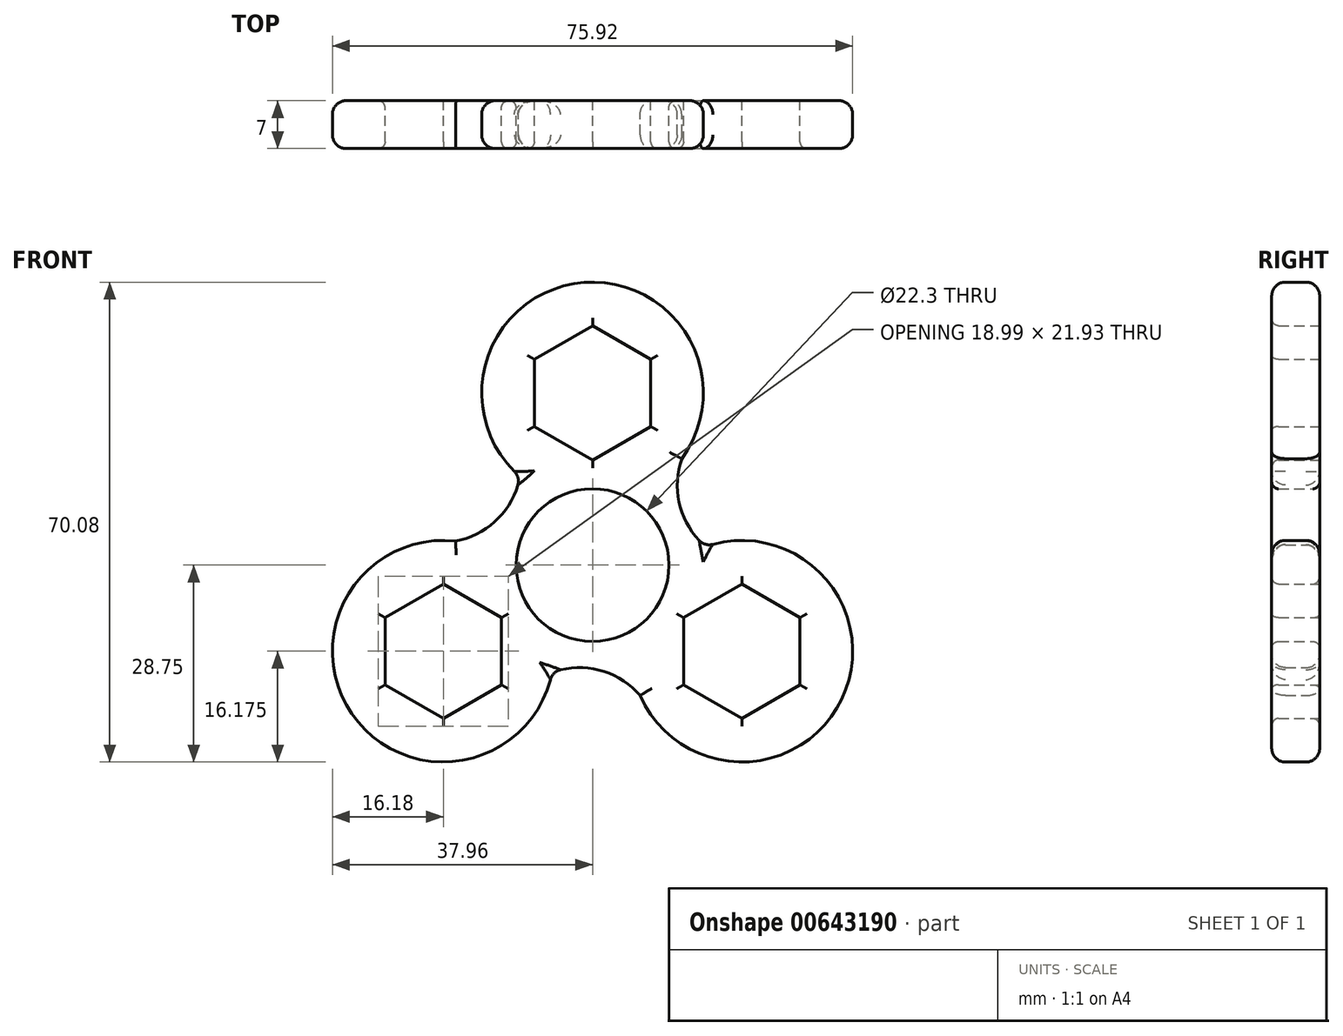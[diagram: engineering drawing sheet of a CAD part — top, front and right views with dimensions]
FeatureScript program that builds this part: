
annotation { "Feature Type Name" : "Feature", "Feature Type Description" : "" }
export const myFeature = defineFeature(function(context is Context, id is Id, definition is map)
    precondition{}
    {
        {
            var Q0;
            Q0=qCreatedBy(makeId("Front.planeOp"),FACE);
            var sketch = newSketch(context, id + "F0", { "sketchPlane" : qUnion([Q0])});
            skLineSegment(sketch, "E0", {"start": v(0, 25) * mm, "end": v(0, 0) * mm});
            skLineSegment(sketch, "E1.1.0", {"start": v(-21.65, -12.5) * mm, "end": v(0, 0) * mm});
            skLineSegment(sketch, "E1.2.0", {"start": v(21.65, -12.5) * mm, "end": v(0, 0) * mm});
            skPoint(sketch, "E1.center", {"position": v(0, 0) * mm});
            skCircle(sketch, "E2", {"center": v(0, 0) * mm, "radius": 11.15 * mm});
            skCircle(sketch, "E3.cCircle", {"center": v(0, 25.15) * mm, "radius": 8.5 * mm, "construction": true});
            skLineSegment(sketch, "E3.0", {"start": v(8.5, 30.05) * mm, "end": v(8.5, 20.24) * mm});
            skLineSegment(sketch, "E3.1", {"start": v(8.5, 20.24) * mm, "end": v(0, 15.34) * mm});
            skLineSegment(sketch, "E3.2", {"start": v(0, 15.34) * mm, "end": v(-8.5, 20.24) * mm});
            skLineSegment(sketch, "E3.3", {"start": v(-8.5, 20.24) * mm, "end": v(-8.5, 30.05) * mm});
            skLineSegment(sketch, "E3.4", {"start": v(-8.5, 30.05) * mm, "end": v(0, 34.96) * mm});
            skLineSegment(sketch, "E3.5", {"start": v(0, 34.96) * mm, "end": v(8.5, 30.05) * mm});
            skPoint(sketch, "E3.0.midPoint", {"position": v(8.5, 25.15) * mm});
            skCircle(sketch, "E4", {"center": v(0, 25.15) * mm, "radius": 16.18 * mm});
            skCircle(sketch, "E5.1.0", {"center": v(-21.78, -12.57) * mm, "radius": 8.5 * mm, "construction": true});
            skCircle(sketch, "E5.1.1", {"center": v(-21.78, -12.57) * mm, "radius": 16.18 * mm});
            skPoint(sketch, "E5.1.2", {"position": v(-26.03, -5.22) * mm});
            skLineSegment(sketch, "E5.1.3", {"start": v(-21.78, -2.77) * mm, "end": v(-13.28, -7.67) * mm});
            skLineSegment(sketch, "E5.1.4", {"start": v(-30.27, -7.67) * mm, "end": v(-21.78, -2.77) * mm});
            skLineSegment(sketch, "E5.1.5", {"start": v(-13.28, -7.67) * mm, "end": v(-13.28, -17.48) * mm});
            skLineSegment(sketch, "E5.1.6", {"start": v(-13.28, -17.48) * mm, "end": v(-21.78, -22.38) * mm});
            skLineSegment(sketch, "E5.1.7", {"start": v(-21.78, -22.38) * mm, "end": v(-30.27, -17.48) * mm});
            skLineSegment(sketch, "E5.1.8", {"start": v(-30.27, -17.48) * mm, "end": v(-30.27, -7.67) * mm});
            skCircle(sketch, "E5.2.0", {"center": v(21.78, -12.57) * mm, "radius": 8.5 * mm, "construction": true});
            skCircle(sketch, "E5.2.1", {"center": v(21.78, -12.57) * mm, "radius": 16.18 * mm});
            skPoint(sketch, "E5.2.2", {"position": v(17.53, -19.93) * mm});
            skLineSegment(sketch, "E5.2.3", {"start": v(13.28, -17.48) * mm, "end": v(13.28, -7.67) * mm});
            skLineSegment(sketch, "E5.2.4", {"start": v(21.78, -22.38) * mm, "end": v(13.28, -17.48) * mm});
            skLineSegment(sketch, "E5.2.5", {"start": v(13.28, -7.67) * mm, "end": v(21.78, -2.77) * mm});
            skLineSegment(sketch, "E5.2.6", {"start": v(21.78, -2.77) * mm, "end": v(30.27, -7.67) * mm});
            skLineSegment(sketch, "E5.2.7", {"start": v(30.27, -7.67) * mm, "end": v(30.27, -17.48) * mm});
            skLineSegment(sketch, "E5.2.8", {"start": v(30.27, -17.48) * mm, "end": v(21.78, -22.38) * mm});
            skArc(sketch, "E6", {"start": v(-19.97, 3.5) * mm, "mid": v(-13.83, 6.77) * mm, "end": v(-10.6, 12.93) * mm});
            skArc(sketch, "E7.1.0", {"start": v(6.95, -19.05) * mm, "mid": v(1.05, -15.36) * mm, "end": v(-5.9, -15.65) * mm});
            skArc(sketch, "E7.2.0", {"start": v(13.02, 15.55) * mm, "mid": v(12.78, 8.6) * mm, "end": v(16.5, 2.72) * mm});
            skSolve(sketch);
        }
        {
            var Q0;
            Q0=makeQuery(id+"F0.imprint","IMPRINT",FACE,{"disambiguationData":[TD([[makeQuery(id+"F0.imprint","IMPRINT",EDGE,{"derivedFrom":sQuery(id+"F0.wireOp",EDGE,"E3.0")}),1.0]])]});
            var Q1;
            {var subQ5=sQuery(id+"F0.wireOp",EDGE,"E7.2.0");Q1=makeQuery(id+"F0.imprint","IMPRINT",FACE,{"disambiguationData":[TD([[makeQuery(id+"F0.imprint","IMPRINT",EDGE,{"derivedFrom":subQ5}),-1.0]])]});}
            var Q2;
            Q2=makeQuery(id+"F0.imprint","IMPRINT",FACE,{"disambiguationData":[TD([[makeQuery(id+"F0.imprint","IMPRINT",EDGE,{"derivedFrom":sQuery(id+"F0.wireOp",EDGE,"E5.2.3")}),1.0]])]});
            var Q3;
            {var subQ5=sQuery(id+"F0.wireOp",EDGE,"E7.1.0");Q3=makeQuery(id+"F0.imprint","IMPRINT",FACE,{"disambiguationData":[TD([[makeQuery(id+"F0.imprint","IMPRINT",EDGE,{"derivedFrom":subQ5}),-1.0]])]});}
            var Q4;
            {var subQ5=sQuery(id+"F0.wireOp",EDGE,"E6");Q4=makeQuery(id+"F0.imprint","IMPRINT",FACE,{"disambiguationData":[TD([[makeQuery(id+"F0.imprint","IMPRINT",EDGE,{"derivedFrom":subQ5}),-1.0]])]});}
            var Q5;
            Q5=makeQuery(id+"F0.imprint","IMPRINT",FACE,{"disambiguationData":[TD([[makeQuery(id+"F0.imprint","IMPRINT",EDGE,{"derivedFrom":sQuery(id+"F0.wireOp",EDGE,"E5.1.3")}),1.0]])]});
            extrude(context, id + "F1", {"entities" : qUnion([Q0, Q1, Q2, Q3, Q4, Q5]), "endBound" : BoundingType.SYMMETRIC, "depth" : 7 * mm, "offsetDistance" : 25 * mm});
        }
        {
            var Q0;
            Q0=makeQuery(id+"F1.opExtrude","CAP_EDGE",EDGE,{"disambiguationData":[OSD([sQuery(id+"F0.wireOp",EDGE,"E4")])],"isStart":true});
            var Q1;
            Q1=makeQuery(id+"F1.opExtrude","CAP_EDGE",EDGE,{"disambiguationData":[OSD([sQuery(id+"F0.wireOp",EDGE,"E7.2.0")])],"isStart":true});
            var Q2;
            Q2=makeQuery(id+"F1.opExtrude","CAP_EDGE",EDGE,{"disambiguationData":[OSD([sQuery(id+"F0.wireOp",EDGE,"E5.2.1")])],"isStart":true});
            var Q3;
            Q3=makeQuery(id+"F1.opExtrude","CAP_EDGE",EDGE,{"disambiguationData":[OSD([sQuery(id+"F0.wireOp",EDGE,"E7.1.0")])],"isStart":true});
            var Q4;
            Q4=makeQuery(id+"F1.opExtrude","CAP_EDGE",EDGE,{"disambiguationData":[OSD([sQuery(id+"F0.wireOp",EDGE,"E5.1.1")])],"isStart":true});
            var Q5;
            Q5=makeQuery(id+"F1.opExtrude","CAP_EDGE",EDGE,{"disambiguationData":[OSD([sQuery(id+"F0.wireOp",EDGE,"E6")])],"isStart":true});
            fillet(context, id + "F2", {"entities" : qUnion([Q0, Q1, Q2, Q3, Q4, Q5]), "radius" : 2 * mm, "tangentPropagation" : true, "allowEdgeOverflow" : false});
        }
        {
            var Q0;
            Q0=makeQuery(id+"F1.opExtrude","CAP_EDGE",EDGE,{"disambiguationData":[OSD([sQuery(id+"F0.wireOp",EDGE,"E7.2.0")])],"isStart":false});
            var Q1;
            Q1=makeQuery(id+"F1.opExtrude","CAP_EDGE",EDGE,{"disambiguationData":[OSD([sQuery(id+"F0.wireOp",EDGE,"E5.2.1")])],"isStart":false});
            var Q2;
            Q2=makeQuery(id+"F1.opExtrude","CAP_EDGE",EDGE,{"disambiguationData":[OSD([sQuery(id+"F0.wireOp",EDGE,"E7.1.0")])],"isStart":false});
            var Q3;
            Q3=makeQuery(id+"F1.opExtrude","CAP_EDGE",EDGE,{"disambiguationData":[OSD([sQuery(id+"F0.wireOp",EDGE,"E5.1.1")])],"isStart":false});
            var Q4;
            Q4=makeQuery(id+"F1.opExtrude","CAP_EDGE",EDGE,{"disambiguationData":[OSD([sQuery(id+"F0.wireOp",EDGE,"E6")])],"isStart":false});
            var Q5;
            Q5=makeQuery(id+"F1.opExtrude","CAP_EDGE",EDGE,{"disambiguationData":[OSD([sQuery(id+"F0.wireOp",EDGE,"E4")])],"isStart":false});
            fillet(context, id + "F3", {"entities" : qUnion([Q0, Q1, Q2, Q3, Q4, Q5]), "radius" : 2 * mm, "tangentPropagation" : true, "allowEdgeOverflow" : false});
        }
        {
            var Q0;
            Q0=makeQuery(id+"F1.opExtrude","SWEPT_EDGE",EDGE,{"disambiguationData":[OSD([sQuery(id+"F0.wireOp",EDGE,"E5.1.1"),sQuery(id+"F0.wireOp",EDGE,"E7.1.0")])]});
            var Q1;
            Q1=makeQuery(id+"F1.opExtrude","SWEPT_EDGE",EDGE,{"disambiguationData":[OSD([sQuery(id+"F0.wireOp",EDGE,"E5.2.1"),sQuery(id+"F0.wireOp",EDGE,"E7.2.0")])]});
            var Q2;
            Q2=makeQuery(id+"F1.opExtrude","SWEPT_EDGE",EDGE,{"disambiguationData":[OSD([sQuery(id+"F0.wireOp",EDGE,"E4"),sQuery(id+"F0.wireOp",EDGE,"E6")])]});
            fillet(context, id + "F4", {"entities" : qUnion([Q0, Q1, Q2]), "radius" : 2 * mm, "tangentPropagation" : true, "allowEdgeOverflow" : false});
        }
        {
            var Q0;
            Q0=makeQuery(id+"F1.opExtrude","CAP_EDGE",EDGE,{"disambiguationData":[OSD([sQuery(id+"F0.wireOp",EDGE,"E2")])],"isStart":false});
            var Q1;
            Q1=makeQuery(id+"F1.opExtrude","CAP_EDGE",EDGE,{"disambiguationData":[OSD([sQuery(id+"F0.wireOp",EDGE,"E3.4")])],"isStart":false});
            var Q2;
            Q2=makeQuery(id+"F1.opExtrude","CAP_EDGE",EDGE,{"disambiguationData":[OSD([sQuery(id+"F0.wireOp",EDGE,"E3.5")])],"isStart":false});
            var Q3;
            Q3=makeQuery(id+"F1.opExtrude","CAP_EDGE",EDGE,{"disambiguationData":[OSD([sQuery(id+"F0.wireOp",EDGE,"E3.3")])],"isStart":false});
            var Q4;
            Q4=makeQuery(id+"F1.opExtrude","CAP_EDGE",EDGE,{"disambiguationData":[OSD([sQuery(id+"F0.wireOp",EDGE,"E3.2")])],"isStart":false});
            var Q5;
            Q5=makeQuery(id+"F1.opExtrude","CAP_EDGE",EDGE,{"disambiguationData":[OSD([sQuery(id+"F0.wireOp",EDGE,"E3.1")])],"isStart":false});
            var Q6;
            Q6=makeQuery(id+"F1.opExtrude","CAP_EDGE",EDGE,{"disambiguationData":[OSD([sQuery(id+"F0.wireOp",EDGE,"E3.0")])],"isStart":false});
            var Q7;
            Q7=makeQuery(id+"F1.opExtrude","CAP_EDGE",EDGE,{"disambiguationData":[OSD([sQuery(id+"F0.wireOp",EDGE,"E5.2.5")])],"isStart":false});
            var Q8;
            Q8=makeQuery(id+"F1.opExtrude","CAP_EDGE",EDGE,{"disambiguationData":[OSD([sQuery(id+"F0.wireOp",EDGE,"E5.2.6")])],"isStart":false});
            var Q9;
            Q9=makeQuery(id+"F1.opExtrude","CAP_EDGE",EDGE,{"disambiguationData":[OSD([sQuery(id+"F0.wireOp",EDGE,"E5.2.3")])],"isStart":false});
            var Q10;
            Q10=makeQuery(id+"F1.opExtrude","CAP_EDGE",EDGE,{"disambiguationData":[OSD([sQuery(id+"F0.wireOp",EDGE,"E5.2.4")])],"isStart":false});
            var Q11;
            Q11=makeQuery(id+"F1.opExtrude","CAP_EDGE",EDGE,{"disambiguationData":[OSD([sQuery(id+"F0.wireOp",EDGE,"E5.2.8")])],"isStart":false});
            var Q12;
            Q12=makeQuery(id+"F1.opExtrude","CAP_EDGE",EDGE,{"disambiguationData":[OSD([sQuery(id+"F0.wireOp",EDGE,"E5.2.7")])],"isStart":false});
            var Q13;
            Q13=makeQuery(id+"F1.opExtrude","CAP_EDGE",EDGE,{"disambiguationData":[OSD([sQuery(id+"F0.wireOp",EDGE,"E5.1.4")])],"isStart":false});
            var Q14;
            Q14=makeQuery(id+"F1.opExtrude","CAP_EDGE",EDGE,{"disambiguationData":[OSD([sQuery(id+"F0.wireOp",EDGE,"E5.1.3")])],"isStart":false});
            var Q15;
            Q15=makeQuery(id+"F1.opExtrude","CAP_EDGE",EDGE,{"disambiguationData":[OSD([sQuery(id+"F0.wireOp",EDGE,"E5.1.8")])],"isStart":false});
            var Q16;
            Q16=makeQuery(id+"F1.opExtrude","CAP_EDGE",EDGE,{"disambiguationData":[OSD([sQuery(id+"F0.wireOp",EDGE,"E5.1.7")])],"isStart":false});
            var Q17;
            Q17=makeQuery(id+"F1.opExtrude","CAP_EDGE",EDGE,{"disambiguationData":[OSD([sQuery(id+"F0.wireOp",EDGE,"E5.1.6")])],"isStart":false});
            var Q18;
            Q18=makeQuery(id+"F1.opExtrude","CAP_EDGE",EDGE,{"disambiguationData":[OSD([sQuery(id+"F0.wireOp",EDGE,"E2")])],"isStart":true});
            var Q19;
            Q19=makeQuery(id+"F1.opExtrude","CAP_EDGE",EDGE,{"disambiguationData":[OSD([sQuery(id+"F0.wireOp",EDGE,"E5.1.6")])],"isStart":true});
            var Q20;
            Q20=makeQuery(id+"F1.opExtrude","CAP_EDGE",EDGE,{"disambiguationData":[OSD([sQuery(id+"F0.wireOp",EDGE,"E5.1.7")])],"isStart":true});
            var Q21;
            Q21=makeQuery(id+"F1.opExtrude","CAP_EDGE",EDGE,{"disambiguationData":[OSD([sQuery(id+"F0.wireOp",EDGE,"E5.1.8")])],"isStart":true});
            var Q22;
            Q22=makeQuery(id+"F1.opExtrude","CAP_EDGE",EDGE,{"disambiguationData":[OSD([sQuery(id+"F0.wireOp",EDGE,"E5.1.4")])],"isStart":true});
            var Q23;
            Q23=makeQuery(id+"F1.opExtrude","CAP_EDGE",EDGE,{"disambiguationData":[OSD([sQuery(id+"F0.wireOp",EDGE,"E5.1.3")])],"isStart":true});
            var Q24;
            Q24=makeQuery(id+"F1.opExtrude","CAP_EDGE",EDGE,{"disambiguationData":[OSD([sQuery(id+"F0.wireOp",EDGE,"E5.1.5")])],"isStart":true});
            var Q25;
            Q25=makeQuery(id+"F1.opExtrude","CAP_EDGE",EDGE,{"disambiguationData":[OSD([sQuery(id+"F0.wireOp",EDGE,"E5.1.5")])],"isStart":false});
            fillet(context, id + "F5", {"entities" : qUnion([Q0, Q1, Q2, Q3, Q4, Q5, Q6, Q7, Q8, Q9, Q10, Q11, Q12, Q13, Q14, Q15, Q16, Q17, Q18, Q19, Q20, Q21, Q22, Q23, Q24, Q25]), "radius" : 1 * mm, "tangentPropagation" : true, "allowEdgeOverflow" : false});
        }
    });
